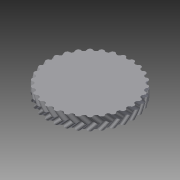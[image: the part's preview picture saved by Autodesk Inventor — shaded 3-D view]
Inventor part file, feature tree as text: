
AUTODESK INVENTOR PART (.ipt)
format: ipt  version: 2013 (Build 170138000, 138)  size: 2,973,184 bytes
history: native  units: mm
features: helix x1, mirror x1, sketch x1
ambient origin geometry x8: Origin, YZ Plane, XZ Plane, XY Plane, X Axis, Y Axis, Z Axis, Center Point
bodies: Solid1 (feature_tree)
feature tree (3):
  helix  "Coil1"  [1 undecoded]
  mirror  "Mirror1"
  sketch  "Sketch1"  dims[d0=314.159265mm d1=7.5mm d2=10.0mm d3=0.0mm d4=90.0deg d5=90.0deg d6=0.0mm d7=0.0mm]
note: 1 required parameter value undecoded (feature->parameter linkage not recoverable at this tier; creation-order binding heuristic only, values carry confidence <= 0.55)
